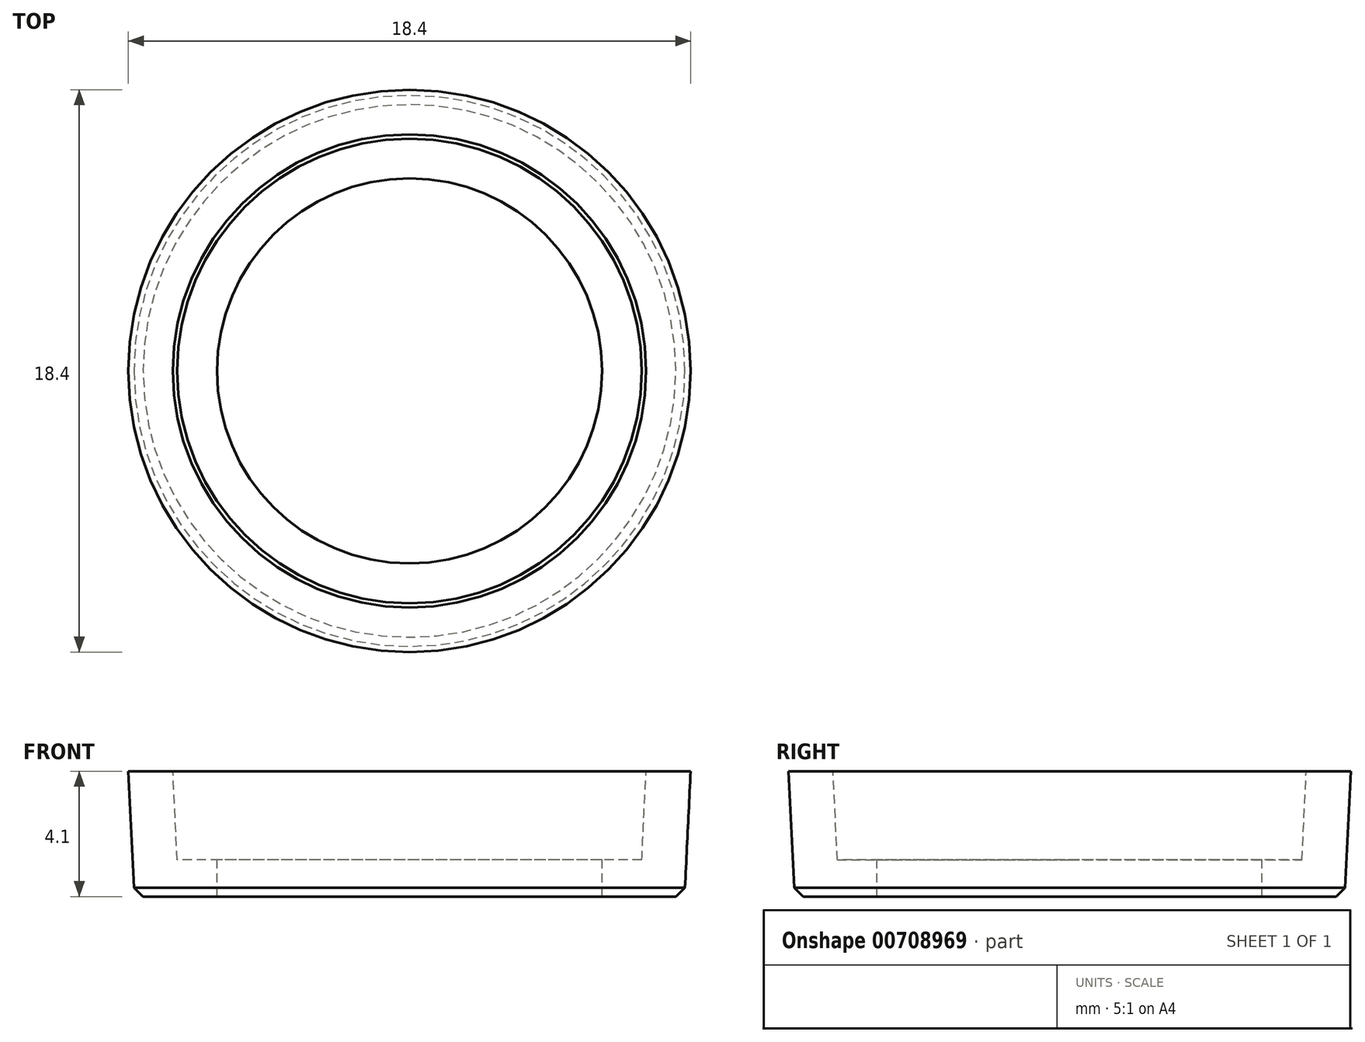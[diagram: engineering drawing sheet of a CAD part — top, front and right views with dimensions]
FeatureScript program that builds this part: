
annotation { "Feature Type Name" : "Feature", "Feature Type Description" : "" }
export const myFeature = defineFeature(function(context is Context, id is Id, definition is map)
    precondition{}
    {
        {
            var Q0;
            Q0=qCreatedBy(makeId("Front.planeOp"),FACE);
            var sketch = newSketch(context, id + "F0", { "sketchPlane" : qUnion([Q0])});
            skLineSegment(sketch, "E0", {"start": v(6.3, 0) * mm, "end": v(9, 0) * mm});
            skLineSegment(sketch, "E1", {"start": v(9, 0) * mm, "end": v(9.2, 4.1) * mm});
            skLineSegment(sketch, "E2", {"start": v(9.2, 4.1) * mm, "end": v(7.74, 4.1) * mm});
            skLineSegment(sketch, "E3", {"start": v(7.74, 4.1) * mm, "end": v(7.6, 1.2) * mm});
            skLineSegment(sketch, "E4", {"start": v(7.6, 1.2) * mm, "end": v(6.3, 1.2) * mm});
            skLineSegment(sketch, "E5", {"start": v(6.3, 1.2) * mm, "end": v(6.3, 0) * mm});
            skLineSegment(sketch, "E6", {"start": v(0, 10.7) * mm, "end": v(0, -3.95) * mm, "construction": true});
            skSolve(sketch);
        }
        {
            var Q0;
            Q0 = qSketchRegion(id + "F0", true);
            var Q1;
            Q1=sQuery(id+"F0.wireOp",EDGE,"E6");
            revolve(context, id + "F1", {"surfaceOperationType" : NewSurfaceOperationType.NEW, "entities" : qUnion([Q0]), "axis" : qUnion([Q1]), "revolveType" : RevolveType.FULL});
        }
        {
            var Q0;
            Q0=makeQuery(id+"F1.opRevolve","SWEPT_EDGE",EDGE,{"disambiguationData":[OSD([sQuery(id+"F0.wireOp",EDGE,"E0"),sQuery(id+"F0.wireOp",EDGE,"E1")])]});
            chamfer(context, id + "F2", {"entities" : qUnion([Q0]), "width" : .3 * mm, "tangentPropagation" : true});
        }
    });
